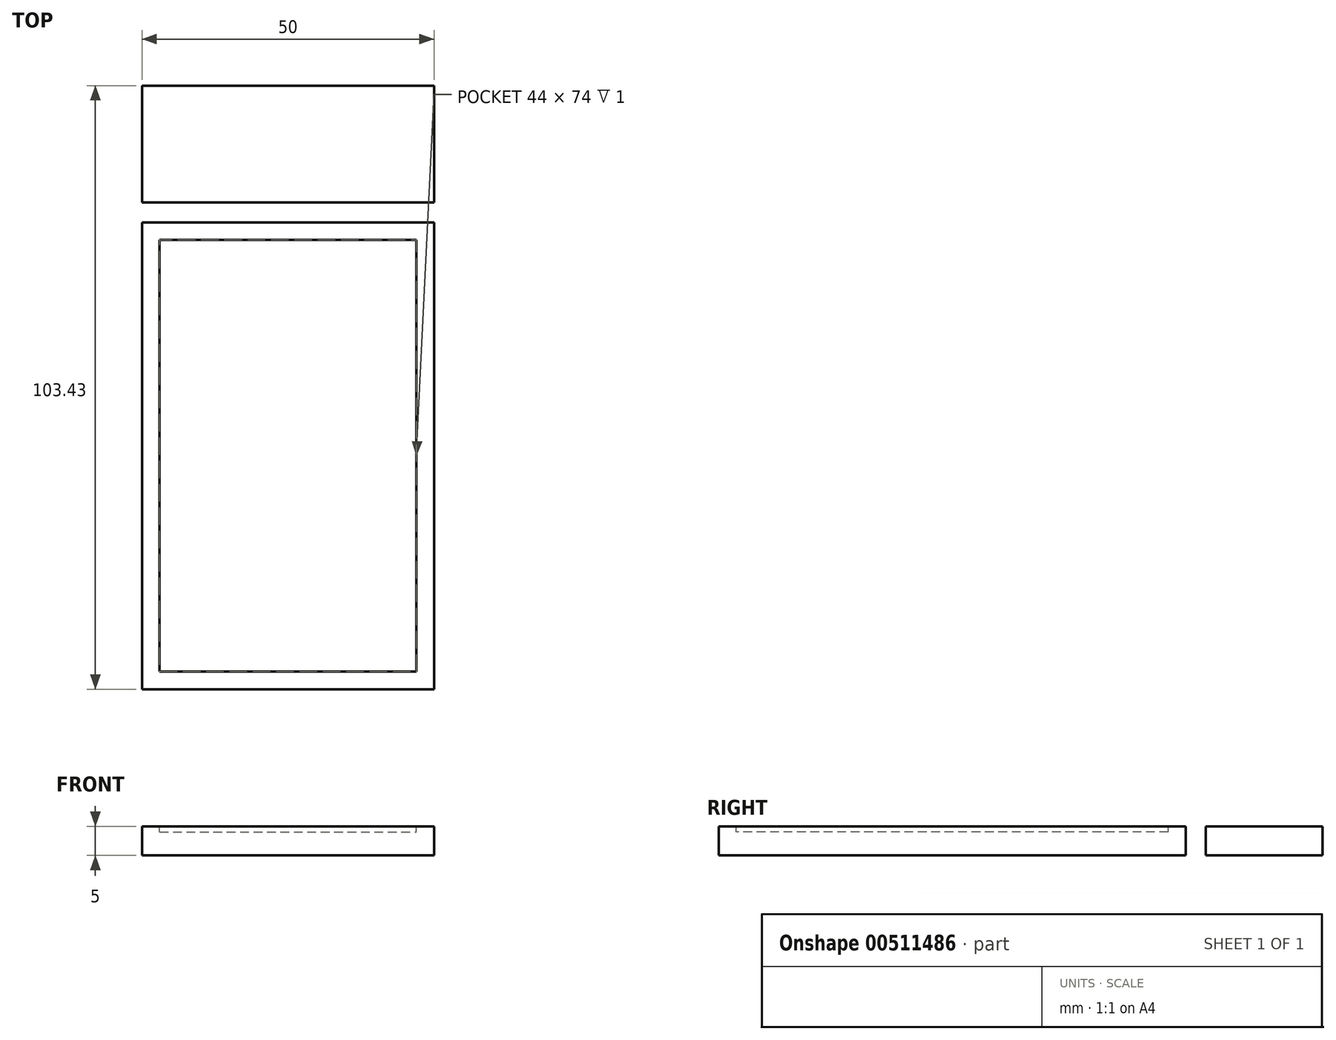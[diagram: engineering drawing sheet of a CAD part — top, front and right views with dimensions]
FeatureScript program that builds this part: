
annotation { "Feature Type Name" : "Feature", "Feature Type Description" : "" }
export const myFeature = defineFeature(function(context is Context, id is Id, definition is map)
    precondition{}
    {
        {
            var Q0;
            Q0=qCreatedBy(makeId("Top.planeOp"),FACE);
            var sketch = newSketch(context, id + "F0", { "sketchPlane" : qUnion([Q0])});
            skLineSegment(sketch, "E0", {"start": v(0, 0) * mm, "end": v(50, 0) * mm});
            skLineSegment(sketch, "E1", {"start": v(50, 0) * mm, "end": v(50, -80) * mm});
            skLineSegment(sketch, "E2", {"start": v(50, -80) * mm, "end": v(0, -80) * mm});
            skLineSegment(sketch, "E3", {"start": v(0, -80) * mm, "end": v(0, 0) * mm});
            skSolve(sketch);
        }
        {
            var Q0;
            Q0=qCreatedBy(makeId("Top.planeOp"),FACE);
            var sketch = newSketch(context, id + "F1", { "sketchPlane" : qUnion([Q0])});
            skLineSegment(sketch, "E4", {"start": v(0, 3.43) * mm, "end": v(50, 3.43) * mm});
            skLineSegment(sketch, "E5", {"start": v(50, 3.43) * mm, "end": v(50, 23.43) * mm});
            skLineSegment(sketch, "E6", {"start": v(50, 23.43) * mm, "end": v(0, 23.43) * mm});
            skLineSegment(sketch, "E7", {"start": v(0, 23.43) * mm, "end": v(0, 3.43) * mm});
            skSolve(sketch);
        }
        {
            var Q0;
            Q0=makeQuery(id+"F0.imprint","IMPRINT",FACE,{"disambiguationData":[TD([[makeQuery(id+"F0.imprint","IMPRINT",EDGE,{"derivedFrom":sQuery(id+"F0.wireOp",EDGE,"E0")}),-1.0]])]});
            extrude(context, id + "F2", {"entities" : qUnion([Q0]), "depth" : 5 * mm});
        }
        {
            var Q0;
            Q0=makeQuery(id+"F1.imprint","IMPRINT",FACE,{"disambiguationData":[TD([[makeQuery(id+"F1.imprint","IMPRINT",EDGE,{"derivedFrom":sQuery(id+"F1.wireOp",EDGE,"E4")}),1.0]])]});
            extrude(context, id + "F3", {"entities" : qUnion([Q0]), "depth" : 5 * mm});
        }
        {
            var Q0;
            Q0=makeQuery(id+"F2.opExtrude","CAP_FACE",FACE,{"disambiguationData":[OSD([sQuery(id+"F0.wireOp",EDGE,"E0"),sQuery(id+"F0.wireOp",EDGE,"E1"),sQuery(id+"F0.wireOp",EDGE,"E2"),sQuery(id+"F0.wireOp",EDGE,"E3")])],"isStart":false});
            var sketch = newSketch(context, id + "F4", { "sketchPlane" : qUnion([Q0])});
            skLineSegment(sketch, "E8.bottom", {"start": v(3, -3) * mm, "end": v(47, -3) * mm});
            skLineSegment(sketch, "E8.top", {"start": v(3, -77) * mm, "end": v(47, -77) * mm});
            skLineSegment(sketch, "E8.left", {"start": v(3, -3) * mm, "end": v(3, -77) * mm});
            skLineSegment(sketch, "E8.right", {"start": v(47, -3) * mm, "end": v(47, -77) * mm});
            skSolve(sketch);
        }
        {
            var Q0;
            Q0=makeQuery(id+"F4.imprint","IMPRINT",FACE,{"disambiguationData":[TD([[makeQuery(id+"F4.imprint","IMPRINT",EDGE,{"derivedFrom":sQuery(id+"F4.wireOp",EDGE,"E8.bottom")}),-1.0]])]});
            extrude(context, id + "F5", {"entities" : qUnion([Q0]), "operationType" : NewBodyOperationType.REMOVE, "oppositeDirection" : true, "depth" : 1 * mm});
        }
    });
